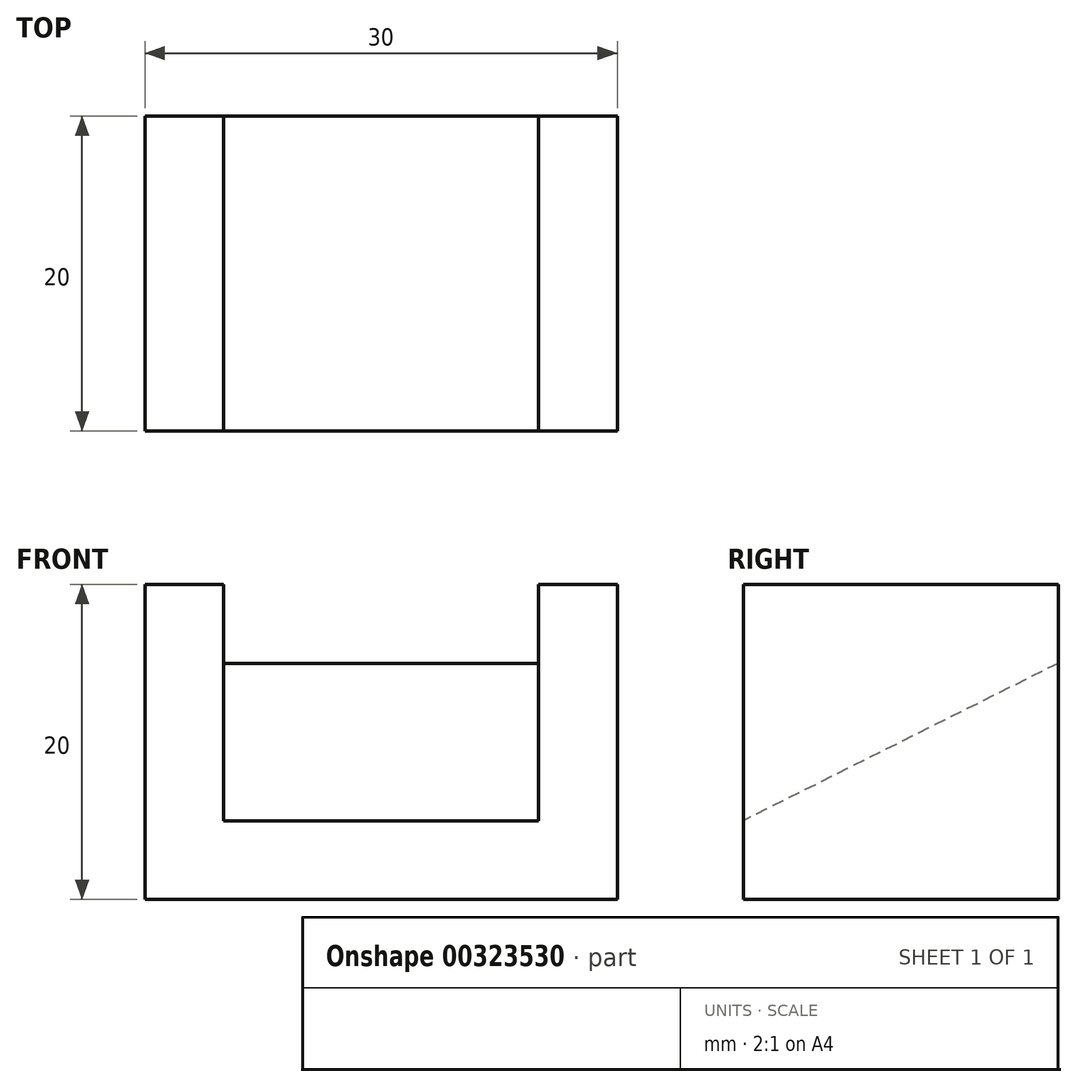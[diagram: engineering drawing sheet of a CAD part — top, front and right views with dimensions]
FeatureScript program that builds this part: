
annotation { "Feature Type Name" : "Feature", "Feature Type Description" : "" }
export const myFeature = defineFeature(function(context is Context, id is Id, definition is map)
    precondition{}
    {
        {
            var Q0;
            Q0=qCreatedBy(makeId("Front.planeOp"),FACE);
            var sketch = newSketch(context, id + "F0", { "sketchPlane" : qUnion([Q0])});
            skLineSegment(sketch, "E0.bottom", {"start": v(0, 0) * mm, "end": v(30, 0) * mm});
            skLineSegment(sketch, "E0.top", {"start": v(0, 20) * mm, "end": v(30, 20) * mm});
            skLineSegment(sketch, "E0.left", {"start": v(0, 0) * mm, "end": v(0, 20) * mm});
            skLineSegment(sketch, "E0.right", {"start": v(30, 0) * mm, "end": v(30, 20) * mm});
            skSolve(sketch);
        }
        {
            var Q0;
            Q0 = qSketchRegion(id + "F0", true);
            extrude(context, id + "F1", {"entities" : qUnion([Q0]), "oppositeDirection" : true, "depth" : 20 * mm});
        }
        {
            var Q0;
            Q0=makeQuery(id+"F1.opExtrude","CAP_FACE",FACE,{"disambiguationData":[OSD([sQuery(id+"F0.wireOp",EDGE,"E0.bottom"),sQuery(id+"F0.wireOp",EDGE,"E0.top"),sQuery(id+"F0.wireOp",EDGE,"E0.left"),sQuery(id+"F0.wireOp",EDGE,"E0.right")])],"isStart":true});
            var sketch = newSketch(context, id + "F2", { "sketchPlane" : qUnion([Q0])});
            skLineSegment(sketch, "E1.bottom", {"start": v(5, 20) * mm, "end": v(25, 20) * mm});
            skLineSegment(sketch, "E1.top", {"start": v(5, 5) * mm, "end": v(25, 5) * mm});
            skLineSegment(sketch, "E1.left", {"start": v(5, 20) * mm, "end": v(5, 5) * mm});
            skLineSegment(sketch, "E1.right", {"start": v(25, 20) * mm, "end": v(25, 5) * mm});
            skSolve(sketch);
        }
        {
            var Q0;
            Q0 = qSketchRegion(id + "F2", true);
            extrude(context, id + "F3", {"entities" : qUnion([Q0]), "operationType" : NewBodyOperationType.REMOVE, "oppositeDirection" : true, "depth" : 25 * mm});
        }
        {
            var Q0;
            Q0=makeQuery(id+"F3.boolean.opBoolean","COPY",FACE,{"derivedFrom":makeQuery(id+"F3.opExtrude","SWEPT_FACE",FACE,{"disambiguationData":[OSD([sQuery(id+"F2.wireOp",EDGE,"E1.left")])]})});
            var sketch = newSketch(context, id + "F4", { "sketchPlane" : qUnion([Q0])});
            skLineSegment(sketch, "E2", {"start": v(0, 5) * mm, "end": v(20, 15) * mm});
            skLineSegment(sketch, "E3", {"start": v(20, 15) * mm, "end": v(20, 5) * mm});
            skLineSegment(sketch, "E4", {"start": v(20, 5) * mm, "end": v(0, 5) * mm});
            skSolve(sketch);
        }
        {
            var Q0;
            Q0 = qSketchRegion(id + "F4", true);
            var Q1;
            Q1=makeQuery(id+"F3.boolean.opBoolean","COPY",FACE,{"derivedFrom":makeQuery(id+"F3.opExtrude","SWEPT_FACE",FACE,{"disambiguationData":[OSD([sQuery(id+"F2.wireOp",EDGE,"E1.right")])]})});
            extrude(context, id + "F5", {"entities" : qUnion([Q0]), "operationType" : NewBodyOperationType.ADD, "endBound" : BoundingType.UP_TO_SURFACE, "endBoundEntityFace" : qUnion([Q1]), "depth" : 25 * mm});
        }
    });
